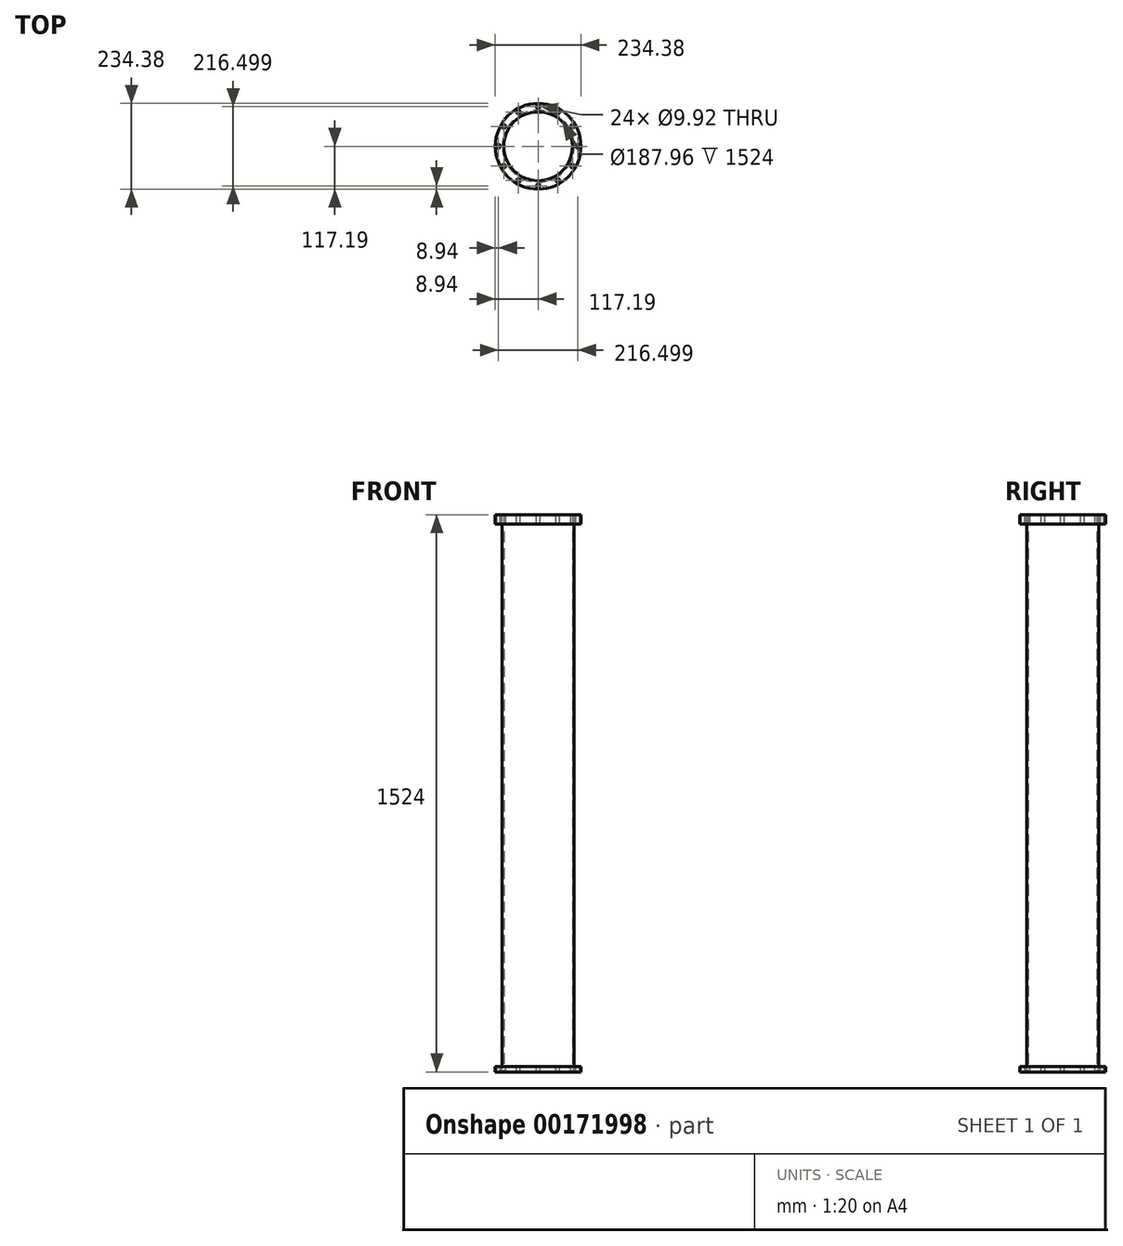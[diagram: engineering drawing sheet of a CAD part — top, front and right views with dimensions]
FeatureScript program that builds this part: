
annotation { "Feature Type Name" : "Feature", "Feature Type Description" : "" }
export const myFeature = defineFeature(function(context is Context, id is Id, definition is map)
    precondition{}
    {
        {
            var Q0;
            Q0=qCreatedBy(makeId("Top.planeOp"),FACE);
            var sketch = newSketch(context, id + "F0", { "sketchPlane" : qUnion([Q0])});
            skCircle(sketch, "E0", {"center": v(0, 0) * mm, "radius": 117.19 * mm});
            skCircle(sketch, "E1", {"center": v(0, 0) * mm, "radius": 98.47 * mm});
            skSolve(sketch);
        }
        {
            var Q0;
            Q0=qSketchRegion(id+"F0",true);
            extrude(context, id + "F1", {"entities" : qUnion([Q0]), "depth" : 14.12 * mm});
        }
        {
            var Q0;
            Q0=makeQuery(id+"F1.opExtrude","CAP_FACE",FACE,{"disambiguationData":[OSD([sQuery(id+"F0.wireOp",EDGE,"E0"),sQuery(id+"F0.wireOp",EDGE,"E1")])],"isStart":true});
            var sketch = newSketch(context, id + "F2", { "sketchPlane" : qUnion([Q0])});
            skCircle(sketch, "E2", {"center": v(0, 0) * mm, "radius": 98.49 * mm});
            skCircle(sketch, "E3", {"center": v(0, 0) * mm, "radius": 93.98 * mm});
            skSolve(sketch);
        }
        {
            var Q0;
            Q0=qSketchRegion(id+"F2",true);
            extrude(context, id + "F3", {"entities" : qUnion([Q0]), "operationType" : NewBodyOperationType.ADD, "oppositeDirection" : true, "depth" : 1524 * mm});
        }
        {
            var Q0;
            Q0=makeQuery(id+"F3.opExtrude","CAP_FACE",FACE,{"disambiguationData":[OSD([sQuery(id+"F2.wireOp",EDGE,"E2"),sQuery(id+"F2.wireOp",EDGE,"E3")])],"isStart":false});
            var sketch = newSketch(context, id + "F4", { "sketchPlane" : qUnion([Q0])});
            skCircle(sketch, "E4", {"center": v(0, 0) * mm, "radius": 98.47 * mm});
            skCircle(sketch, "E5", {"center": v(0, 0) * mm, "radius": 117.19 * mm});
            skSolve(sketch);
        }
        {
            var Q0;
            Q0=qSketchRegion(id+"F4",true);
            extrude(context, id + "F5", {"entities" : qUnion([Q0]), "operationType" : NewBodyOperationType.ADD, "oppositeDirection" : true, "depth" : 25.4 * mm});
        }
        {
            var Q0;
            Q0=makeQuery(id+"F5.boolean.opBoolean","MERGE",FACE,{"derivedFrom":[makeQuery(id+"F3.opExtrude","CAP_FACE",FACE,{"disambiguationData":[OSD([sQuery(id+"F2.wireOp",EDGE,"E2"),sQuery(id+"F2.wireOp",EDGE,"E3")])],"isStart":false}),makeQuery(id+"F5.opExtrude","CAP_FACE",FACE,{"disambiguationData":[OSD([sQuery(id+"F4.wireOp",EDGE,"E4"),sQuery(id+"F4.wireOp",EDGE,"E5")])],"isStart":true})]});
            var sketch = newSketch(context, id + "F6", { "sketchPlane" : qUnion([Q0])});
            skCircle(sketch, "E6", {"center": v(0, -108.25) * mm, "radius": 4.96 * mm});
            skCircle(sketch, "E7.1.0", {"center": v(54.12, -93.75) * mm, "radius": 4.96 * mm});
            skCircle(sketch, "E7.2.0", {"center": v(93.75, -54.12) * mm, "radius": 4.96 * mm});
            skCircle(sketch, "E7.3.0", {"center": v(108.25, 0) * mm, "radius": 4.96 * mm});
            skCircle(sketch, "E7.4.0", {"center": v(93.75, 54.12) * mm, "radius": 4.96 * mm});
            skCircle(sketch, "E7.5.0", {"center": v(54.12, 93.75) * mm, "radius": 4.96 * mm});
            skCircle(sketch, "E7.6.0", {"center": v(0, 108.25) * mm, "radius": 4.96 * mm});
            skCircle(sketch, "E7.7.0", {"center": v(-54.12, 93.75) * mm, "radius": 4.96 * mm});
            skCircle(sketch, "E7.8.0", {"center": v(-93.75, 54.12) * mm, "radius": 4.96 * mm});
            skCircle(sketch, "E7.9.0", {"center": v(-108.25, 0) * mm, "radius": 4.96 * mm});
            skCircle(sketch, "E7.10.0", {"center": v(-93.75, -54.12) * mm, "radius": 4.96 * mm});
            skCircle(sketch, "E7.11.0", {"center": v(-54.12, -93.75) * mm, "radius": 4.96 * mm});
            skPoint(sketch, "E7.center", {"position": v(0, 0) * mm});
            skSolve(sketch);
        }
        {
            var Q0;
            Q0=qSketchRegion(id+"F6",true);
            extrude(context, id + "F7", {"entities" : qUnion([Q0]), "operationType" : NewBodyOperationType.REMOVE, "endBound" : BoundingType.THROUGH_ALL, "oppositeDirection" : true, "depth" : 25.4 * mm});
        }
    });
